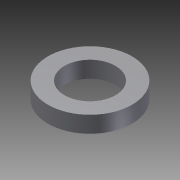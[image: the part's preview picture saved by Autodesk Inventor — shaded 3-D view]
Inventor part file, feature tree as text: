
AUTODESK INVENTOR PART (.ipt)
format: ipt  version: 2014 SP2 (Build 180246200, 246)  size: 96,768 bytes
history: native  units: in
note: dims shown in document units (in); Inventor stores cm internally (conversion verified against a paired STEP export)
features: extrude x2, sketch x2, other x1, imported_body x1
ambient origin geometry x8: Origin, YZ Plane, XZ Plane, XY Plane, X Axis, Y Axis, Z Axis, Center Point
bodies: Body1 (feature_tree)
feature tree (6):
  parser-record x1  (decoder bookkeeping rows leaked as tree rows — omitted from the tree; the rows remain in map.json)
  imported_body  "Base1"
  extrude  "Extrusion1"  Depth=1.0in TaperAngle=0.0deg
  extrude  "Extrusion2"  [1 undecoded]
  sketch  "Sketch1"  dims[d0=0.32in d1=1.0in d2=0.0in]
  sketch  "Sketch2"  dims[d3=0.4375in d4=0.0in]
note: 1 required parameter value undecoded (feature->parameter linkage not recoverable at this tier; creation-order binding heuristic only, values carry confidence <= 0.55)
